# Revit family: Hager-SM_Design_30-Switch_Disc.Incomer-NoHosted-UK-en
name_source: partatom
category: Electrical Equipment
units: mm (PartAtom-declared; Revit-internal decimal feet)

## family parameters
Always vertical = Yes
Cut with Voids When Loaded = No
Panel Configuration = Two Columns, Circuits Across
Part Type = Panelboard
Room Calculation Point = No
Round Connector Dimension = Use Diameter
Shared = No
Work Plane-Based = Yes

## types (12) — shared parameters
Classification.Uniclass.Pr.Description = Control circuit device enclosures
Classification.Uniclass.Pr.Number = Pr_80_77_28_16
Default Elevation = 1219 mm
EF000003 - Mounting method = EV000384 - Surface mounted (plaster)
EF000007 - Colour = EV000202 - White
EF000040 - Height = 240 mm  [stored 0.787402 ft]
EF000049 - Depth = 102 mm
EF000116 - RAL-number = 9010
EF000118 - With mounting plate = No
EF000266 - Number of rows = 1
EF000339 - Type of cover = EV004216 - Door
EF001062 - EMC-version = No
EF001088 - Extension possible = No
EF001134 - DIN-rail = No
EF001596 - Material housing = EV000179 - Steel
EF004462 - Type of closure = EV000154 - Other
EF005474 - Degree of protection (IP) = EV009848 - IP2XC
EF006244 - Transparent cover/door = No
EF006306 - With lock = No
EF015776 - Earthing terminal block = Yes
EF015777 - Neutral terminal block = Yes
EF015941 - Signal passing door = No
HG000002 - With door or cover = Yes
HG000003 - Range = Surface Mounting Consumer Units
HG000005 - Thickness = 3 mm  [stored 0.00984252 ft]
HG000006 - Flush mounted = No
HG000017 - Distance between poles = 18 mm  [stored 0.0590551 ft]
Manufacturer = Hager
Type Comments = Surface Mounting Consumer Units
zero-valued in all types: Cost, EF000218 - Built-in depth, EF000332 - Built-in height, EF000846 - Built-in width, EF001131 - Internal depth

## per-type parameters (varying)
| type | EF000008 - Width | EF002950 - Width in number of modular spacings | HG000004 - Manufacturer reference | Model |
| Surface mounted P2XC W149 H240 D102 4 Modular spacings - VM004 | 149 mm  [stored 0.488845 ft] | 4 | VM004 | VM004 |
| Surface mounted P2XC W149 H240 D102 4 Modular spacings - VM004K | 149 mm  [stored 0.488845 ft] | 4 | VM004K | VM004K |
| Surface mounted P2XC W221 H240 D102 8 Modular spacings - VM008 | 221 mm  [stored 0.725066 ft] | 8 | VM008 | VM008 |
| Surface mounted P2XC W221 H240 D102 8 Modular spacings - VM008K | 221 mm  [stored 0.725066 ft] | 8 | VM008K | VM008K |
| Surface mounted P2XC W292 H240 D102 12 Modular spacings - VM012 | 292 mm  [stored 0.958005 ft] | 12 | VM012 | VM012 |
| Surface mounted P2XC W292 H240 D102 12 Modular spacings - VM012K | 292 mm  [stored 0.958005 ft] | 12 | VM012K | VM012K |
| Surface mounted P2XC W364 H240 D102 16 Modular spacings - VM016 | 364 mm  [stored 1.19423 ft] | 16 | VM016 | VM016 |
| Surface mounted P2XC W364 H240 D102 16 Modular spacings - VM016K | 364 mm  [stored 1.19423 ft] | 16 | VM016K | VM016K |
| Surface mounted P2XC W471 H240 D102 18 Modular spacings - VM018K | 471 mm  [stored 1.54528 ft] | 18 | VM018K | VM018K |
| Surface mounted P2XC W471 H240 D102 22 Modular spacings - VM022K | 471 mm  [stored 1.54528 ft] | 22 | VM022K | VM022K |
| Surface mounted P2XC W472 H240 D102 18 Modular spacings - VM018 | 472 mm | 18 | VM018 | VM018 |
| Surface mounted P2XC W472 H240 D102 22 Modular spacings - VM022 | 472 mm | 22 | VM022 | VM022 |

note: [stored X ft] marks values corroborated as IEEE doubles in the binary element streams (Revit-internal decimal feet)

## geometry (parser evidence)
native form markers: Blend x4, Sweep x13
no freeform markers — native parametric forms only
